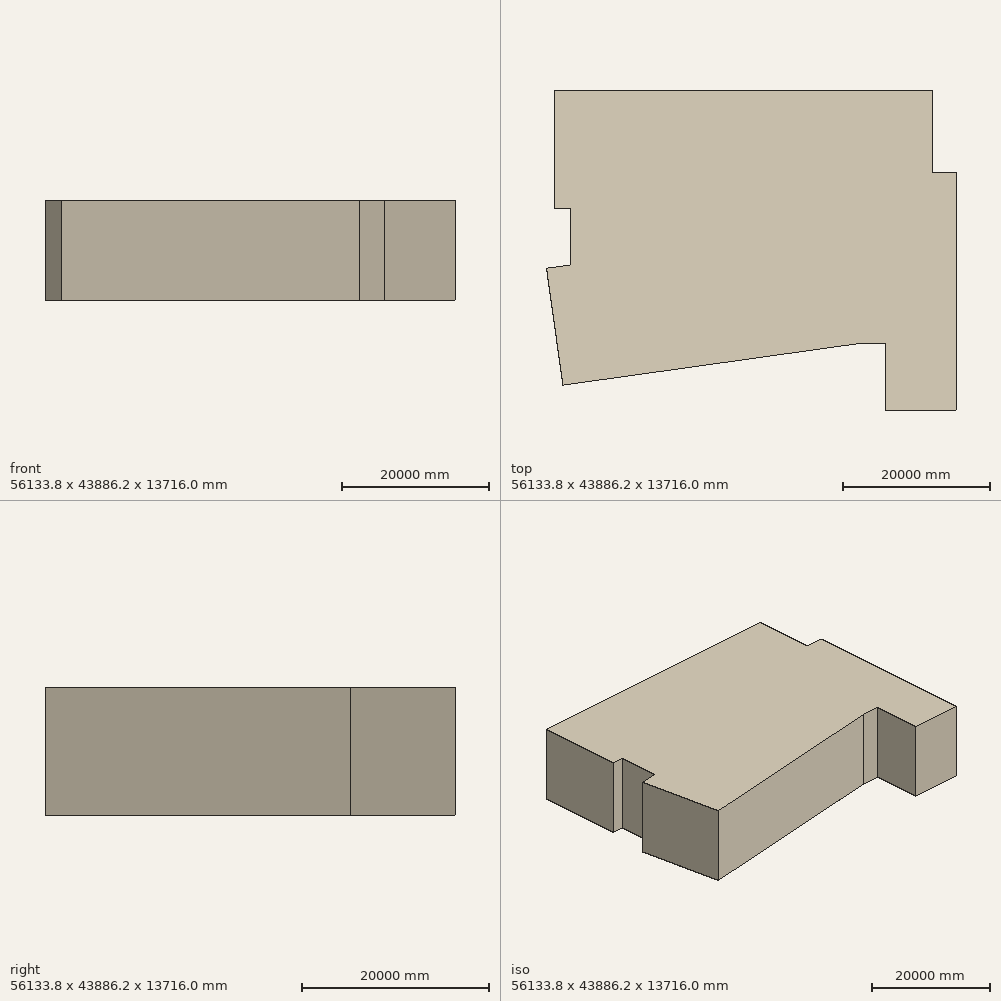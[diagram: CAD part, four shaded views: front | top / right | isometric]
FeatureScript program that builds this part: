
annotation { "Feature Type Name" : "Feature", "Feature Type Description" : "" }
export const myFeature = defineFeature(function(context is Context, id is Id, definition is map)
    precondition{}
    {
        {
            var Q0;
            Q0=qCreatedBy(makeId("Top.planeOp"),FACE);
            var sketch = newSketch(context, id + "F0", { "sketchPlane" : qUnion([Q0])});
            skLineSegment(sketch, "E0.bottom", {"start": v(-41605.2, 16154.4) * mm, "end": v(0, 16154.4) * mm});
            skLineSegment(sketch, "E0.top", {"start": v(-41605.2, 0) * mm, "end": v(-39444, 0) * mm});
            skLineSegment(sketch, "E0.left", {"start": v(-41605.2, 16154.4) * mm, "end": v(-41605.2, 0) * mm});
            skLineSegment(sketch, "E1.bottom", {"start": v(0, 16154.4) * mm, "end": v(10058.4, 16154.4) * mm});
            skLineSegment(sketch, "E2", {"start": v(273.19, -18503.67) * mm, "end": v(-40474.36, -24230.37) * mm});
            skLineSegment(sketch, "E3", {"start": v(-40474.36, -24230.37) * mm, "end": v(-42722.62, -8233.18) * mm});
            skLineSegment(sketch, "E4", {"start": v(-42722.62, -8233.18) * mm, "end": v(-39444, -7772.4) * mm});
            skLineSegment(sketch, "E5", {"start": v(-39444, -7772.4) * mm, "end": v(-39444, 0) * mm});
            skLineSegment(sketch, "E6.bottom", {"start": v(10058.4, 4876.8) * mm, "end": v(13411.2, 4876.8) * mm});
            skLineSegment(sketch, "E6.right", {"start": v(13411.2, 4876.8) * mm, "end": v(13411.2, -27731.79) * mm});
            skLineSegment(sketch, "E7", {"start": v(10058.4, 16154.4) * mm, "end": v(10058.4, 4876.8) * mm});
            skLineSegment(sketch, "E8", {"start": v(273.19, -18503.67) * mm, "end": v(3625.99, -18503.67) * mm});
            skLineSegment(sketch, "E9", {"start": v(3625.99, -18503.67) * mm, "end": v(3625.99, -27731.79) * mm});
            skLineSegment(sketch, "E10", {"start": v(3625.99, -27731.79) * mm, "end": v(13411.2, -27731.79) * mm});
            skPoint(sketch, "E0.right.end.orphan", {"position": v(0, 0) * mm});
            skSolve(sketch);
        }
        {
            var Q0;
            Q0 = qSketchRegion(id + "F0", true);
            extrude(context, id + "F1", {"entities" : qUnion([Q0]), "depth" : 13716 * mm, "offsetDistance" : 25.4 * mm});
        }
    });
